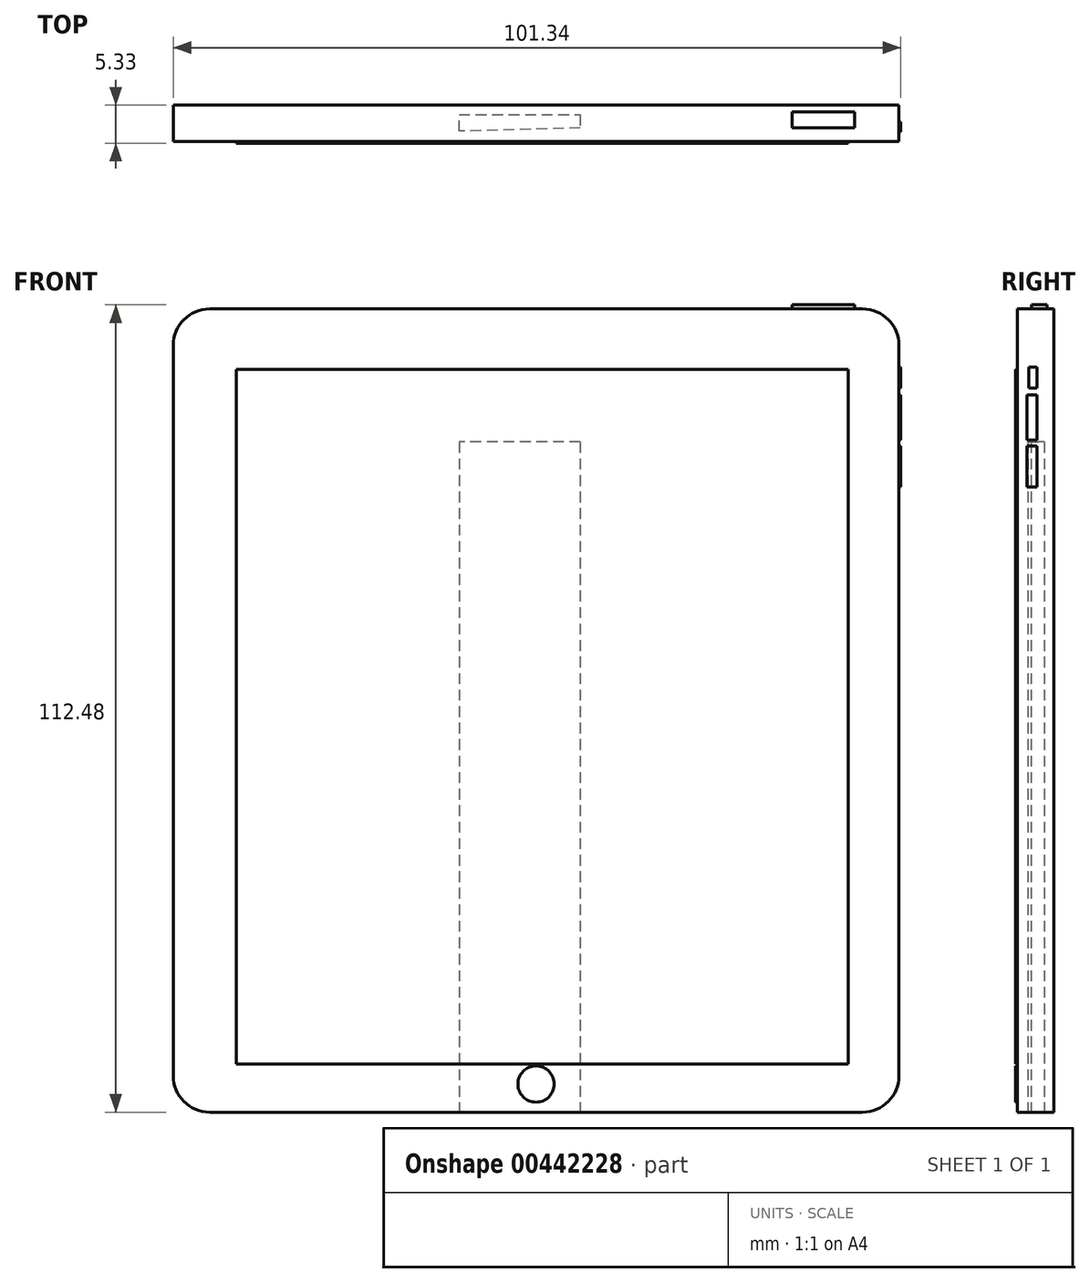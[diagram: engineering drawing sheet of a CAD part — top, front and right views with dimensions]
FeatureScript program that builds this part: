
annotation { "Feature Type Name" : "Feature", "Feature Type Description" : "" }
export const myFeature = defineFeature(function(context is Context, id is Id, definition is map)
    precondition{}
    {
        {
            var Q0;
            Q0=qCreatedBy(makeId("Front.planeOp"),FACE);
            var sketch = newSketch(context, id + "F0", { "sketchPlane" : qUnion([Q0])});
            skLineSegment(sketch, "E0.bottom", {"start": v(-45.46, 55.95) * mm, "end": v(45.46, 55.95) * mm});
            skLineSegment(sketch, "E0.top", {"start": v(-45.46, -55.95) * mm, "end": v(45.46, -55.95) * mm});
            skLineSegment(sketch, "E0.left", {"start": v(-50.54, 50.87) * mm, "end": v(-50.54, -50.87) * mm});
            skLineSegment(sketch, "E0.right", {"start": v(50.54, 50.87) * mm, "end": v(50.54, -50.87) * mm});
            skPoint(sketch, "E0.middle", {"position": v(0, 0) * mm});
            skPoint(sketch, "E1.visualSharp", {"position": v(-50.54, 55.95) * mm});
            skArc(sketch, "E1.filletArc", {"start": v(-45.46, 55.95) * mm, "mid": v(-49.05, 54.46) * mm, "end": v(-50.54, 50.87) * mm});
            skPoint(sketch, "E2.visualSharp", {"position": v(50.54, 55.95) * mm});
            skArc(sketch, "E2.filletArc", {"start": v(50.54, 50.87) * mm, "mid": v(49.05, 54.46) * mm, "end": v(45.46, 55.95) * mm});
            skPoint(sketch, "E3.visualSharp", {"position": v(50.54, -55.95) * mm});
            skArc(sketch, "E3.filletArc", {"start": v(45.46, -55.95) * mm, "mid": v(49.05, -54.46) * mm, "end": v(50.54, -50.87) * mm});
            skPoint(sketch, "E4.visualSharp", {"position": v(-50.54, -55.95) * mm});
            skArc(sketch, "E4.filletArc", {"start": v(-50.54, -50.87) * mm, "mid": v(-49.05, -54.46) * mm, "end": v(-45.46, -55.95) * mm});
            skCircle(sketch, "E5", {"center": v(0, -50.88) * mm, "radius": 2.74 * mm});
            skCircle(sketch, "E6", {"center": v(0, 50.88) * mm, "radius": 1.1 * mm});
            skSolve(sketch);
        }
        {
            var Q0;
            Q0 = qSketchRegion(id + "F0", true);
            var Q1;
            Q1=makeQuery(id+"F0.imprint","IMPRINT",FACE,{"disambiguationData":[TD([[makeQuery(id+"F0.imprint","IMPRINT",EDGE,{"derivedFrom":sQuery(id+"F0.wireOp",EDGE,"jizpzQJK-FtYb-snMM-lDZa-Pu40AYu2MoG9.bottom")}),-1.0]])]});
            var Q2;
            Q2=makeQuery(id+"F0.imprint","IMPRINT",FACE,{"disambiguationData":[TD([[makeQuery(id+"F0.imprint","IMPRINT",EDGE,{"derivedFrom":sQuery(id+"F0.wireOp",EDGE,"E5")}),1.0]])]});
            var Q3;
            Q3=makeQuery(id+"F0.imprint","IMPRINT",FACE,{"disambiguationData":[TD([[makeQuery(id+"F0.imprint","IMPRINT",EDGE,{"derivedFrom":sQuery(id+"F0.wireOp",EDGE,"E6")}),1.0]])]});
            extrude(context, id + "F1", {"entities" : qUnion([Q0, Q1, Q2, Q3]), "depth" : 5.08 * mm});
        }
        {
            var Q0;
            Q0=makeQuery(id+"F1.opExtrude","CAP_FACE",FACE,{"disambiguationData":[OSD([sQuery(id+"F0.wireOp",EDGE,"E0.bottom"),sQuery(id+"F0.wireOp",EDGE,"E0.top"),sQuery(id+"F0.wireOp",EDGE,"E0.left"),sQuery(id+"F0.wireOp",EDGE,"E0.right"),sQuery(id+"F0.wireOp",EDGE,"E1.filletArc"),sQuery(id+"F0.wireOp",EDGE,"E2.filletArc"),sQuery(id+"F0.wireOp",EDGE,"E3.filletArc"),sQuery(id+"F0.wireOp",EDGE,"E4.filletArc")])],"isStart":false});
            var sketch = newSketch(context, id + "F2", { "sketchPlane" : qUnion([Q0])});
            skLineSegment(sketch, "E7.bottom", {"start": v(-41.78, 47.56) * mm, "end": v(43.46, 47.56) * mm});
            skLineSegment(sketch, "E7.top", {"start": v(-41.78, -49.24) * mm, "end": v(43.46, -49.24) * mm});
            skLineSegment(sketch, "E7.left", {"start": v(-41.78, 47.56) * mm, "end": v(-41.78, -49.24) * mm});
            skLineSegment(sketch, "E7.right", {"start": v(43.46, 47.56) * mm, "end": v(43.46, -49.24) * mm});
            skCircle(sketch, "E8", {"center": v(0, -52.4) * mm, "radius": 2.27 * mm});
            skSolve(sketch);
        }
        {
            var Q0;
            Q0=makeQuery(id+"F2.imprint","IMPRINT",FACE,{"disambiguationData":[TD([[makeQuery(id+"F2.imprint","IMPRINT",EDGE,{"derivedFrom":sQuery(id+"F2.wireOp",EDGE,"E7.bottom")}),-1.0]])]});
            extrude(context, id + "F3", {"entities" : qUnion([Q0]), "operationType" : NewBodyOperationType.ADD, "depth" : 0.25 * mm});
        }
        {
            var Q0;
            Q0=makeQuery(id+"F1.opExtrude","SWEPT_FACE",FACE,{"disambiguationData":[OSD([sQuery(id+"F0.wireOp",EDGE,"E0.top")])]});
            var sketch = newSketch(context, id + "F4", { "sketchPlane" : qUnion([Q0])});
            skLineSegment(sketch, "E9", {"start": v(-10.72, 3.63) * mm, "end": v(-10.72, 1.34) * mm});
            skLineSegment(sketch, "E10", {"start": v(6.15, 1.34) * mm, "end": v(6.15, 3.19) * mm});
            skLineSegment(sketch, "E11", {"start": v(6.15, 3.19) * mm, "end": v(-10.72, 3.63) * mm});
            skLineSegment(sketch, "E12", {"start": v(-10.72, 1.34) * mm, "end": v(6.15, 1.34) * mm});
            skCircle(sketch, "E13", {"center": v(-40.95, 2.46) * mm, "radius": 1.96 * mm});
            skCircle(sketch, "E14", {"center": v(-35.96, 2.6) * mm, "radius": 1.7 * mm});
            skCircle(sketch, "E15", {"center": v(-31.16, 2.6) * mm, "radius": 1.58 * mm});
            skCircle(sketch, "E16", {"center": v(-26.62, 2.53) * mm, "radius": 1.52 * mm});
            skSolve(sketch);
        }
        {
            var Q0;
            Q0 = qSketchRegion(id + "F4", true);
            var sketch = newSketch(context, id + "F5", { "sketchPlane" : qUnion([Q0])});
            skSolve(sketch);
        }
        {
            var Q0;
            Q0=makeQuery(id+"F4.imprint","IMPRINT",FACE,{"disambiguationData":[TD([[makeQuery(id+"F4.imprint","IMPRINT",EDGE,{"derivedFrom":sQuery(id+"F4.wireOp",EDGE,"E9")}),1.0]])]});
            var Q1;
            Q1=makeQuery(id+"F5.imprint","IMPRINT",FACE,{"disambiguationData":[TD([[makeQuery(id+"F5.imprint","IMPRINT",EDGE,{"derivedFrom":makeQuery(id+"F4.imprint","IMPRINT",EDGE,{"derivedFrom":sQuery(id+"F4.wireOp",EDGE,"E13")})}),1.0]])]});
            var Q2;
            Q2=makeQuery(id+"F5.imprint","IMPRINT",FACE,{"disambiguationData":[TD([[makeQuery(id+"F5.imprint","IMPRINT",EDGE,{"derivedFrom":makeQuery(id+"F4.imprint","IMPRINT",EDGE,{"derivedFrom":sQuery(id+"F4.wireOp",EDGE,"E14")})}),1.0]])]});
            var Q3;
            Q3=makeQuery(id+"F5.imprint","IMPRINT",FACE,{"disambiguationData":[TD([[makeQuery(id+"F5.imprint","IMPRINT",EDGE,{"derivedFrom":makeQuery(id+"F4.imprint","IMPRINT",EDGE,{"derivedFrom":sQuery(id+"F4.wireOp",EDGE,"E15")})}),1.0]])]});
            var Q4;
            Q4=makeQuery(id+"F5.imprint","IMPRINT",FACE,{"disambiguationData":[TD([[makeQuery(id+"F5.imprint","IMPRINT",EDGE,{"derivedFrom":makeQuery(id+"F4.imprint","IMPRINT",EDGE,{"derivedFrom":sQuery(id+"F4.wireOp",EDGE,"E16")})}),1.0]])]});
            var Q5;
            Q5=sQuery(id+"F4.wireOp",EDGE,"E11");
            var Q6;
            Q6=sQuery(id+"F4.wireOp",EDGE,"E9");
            var Q7;
            Q7=sQuery(id+"F4.wireOp",EDGE,"E10");
            var Q8;
            Q8=sQuery(id+"F4.wireOp",EDGE,"E12");
            extrude(context, id + "F6", {"entities" : qUnion([Q0, Q1, Q2, Q3, Q4]), "surfaceEntities" : qUnion([Q5, Q6, Q7, Q8]), "oppositeDirection" : true, "depth" : 93.35 * mm});
        }
        {
            var Q0;
            Q0=makeQuery(id+"F1.opExtrude","SWEPT_FACE",FACE,{"disambiguationData":[OSD([sQuery(id+"F0.wireOp",EDGE,"E0.bottom")])]});
            var sketch = newSketch(context, id + "F7", { "sketchPlane" : qUnion([Q0])});
            skCircle(sketch, "E17", {"center": v(-41, -2.61) * mm, "radius": 1.52 * mm});
            skLineSegment(sketch, "E18.bottom", {"start": v(44.36, -0.97) * mm, "end": v(35.64, -0.97) * mm});
            skLineSegment(sketch, "E18.top", {"start": v(44.36, -3.16) * mm, "end": v(35.64, -3.16) * mm});
            skLineSegment(sketch, "E18.left", {"start": v(44.36, -0.97) * mm, "end": v(44.36, -3.16) * mm});
            skLineSegment(sketch, "E18.right", {"start": v(35.64, -0.97) * mm, "end": v(35.64, -3.16) * mm});
            skLineSegment(sketch, "E19.bottom", {"start": v(-1.77, -3.7) * mm, "end": v(2.1, -3.7) * mm});
            skLineSegment(sketch, "E19.top", {"start": v(-1.77, -3.1) * mm, "end": v(2.1, -3.1) * mm});
            skLineSegment(sketch, "E19.left", {"start": v(-1.77, -3.7) * mm, "end": v(-1.77, -3.1) * mm});
            skLineSegment(sketch, "E19.right", {"start": v(2.1, -3.7) * mm, "end": v(2.1, -3.1) * mm});
            skSolve(sketch);
        }
        {
            var Q0;
            Q0=makeQuery(id+"F7.imprint","IMPRINT",FACE,{"disambiguationData":[TD([[makeQuery(id+"F7.imprint","IMPRINT",EDGE,{"derivedFrom":sQuery(id+"F7.wireOp",EDGE,"E18.bottom")}),1.0]])]});
            var Q1;
            Q1=sQuery(id+"F7.wireOp",EDGE,"E18.bottom");
            var Q2;
            Q2=sQuery(id+"F7.wireOp",EDGE,"E18.left");
            var Q3;
            Q3=sQuery(id+"F7.wireOp",EDGE,"E18.top");
            var Q4;
            Q4=sQuery(id+"F7.wireOp",EDGE,"E18.right");
            extrude(context, id + "F8", {"entities" : qUnion([Q0]), "operationType" : NewBodyOperationType.ADD, "surfaceEntities" : qUnion([Q1, Q2, Q3, Q4]), "depth" : 0.57 * mm});
        }
        {
            var Q0;
            Q0=makeQuery(id+"F1.opExtrude","CAP_FACE",FACE,{"disambiguationData":[OSD([sQuery(id+"F0.wireOp",EDGE,"E0.bottom"),sQuery(id+"F0.wireOp",EDGE,"E0.top"),sQuery(id+"F0.wireOp",EDGE,"E0.left"),sQuery(id+"F0.wireOp",EDGE,"E0.right"),sQuery(id+"F0.wireOp",EDGE,"E1.filletArc"),sQuery(id+"F0.wireOp",EDGE,"E2.filletArc"),sQuery(id+"F0.wireOp",EDGE,"E3.filletArc"),sQuery(id+"F0.wireOp",EDGE,"E4.filletArc")])],"isStart":false});
            var sketch = newSketch(context, id + "F9", { "sketchPlane" : qUnion([Q0])});
            skCircle(sketch, "E20", {"center": v(0, -52.03) * mm, "radius": 2.53 * mm});
            skPoint(sketch, "E20.centerSnap0", {"position": v(0, -55.95) * mm});
            skSolve(sketch);
        }
        {
            var Q0;
            Q0 = qSketchRegion(id + "F9", true);
            extrude(context, id + "F10", {"entities" : qUnion([Q0]), "operationType" : NewBodyOperationType.ADD, "depth" : 0.25 * mm});
        }
        {
            var Q0;
            Q0=makeQuery(id+"F1.opExtrude","SWEPT_FACE",FACE,{"disambiguationData":[OSD([sQuery(id+"F0.wireOp",EDGE,"E0.right")])]});
            var sketch = newSketch(context, id + "F11", { "sketchPlane" : qUnion([Q0])});
            skLineSegment(sketch, "E21.bottom", {"start": v(-3.74, 44) * mm, "end": v(-2.37, 44) * mm});
            skLineSegment(sketch, "E21.top", {"start": v(-3.74, 37.7) * mm, "end": v(-2.37, 37.7) * mm});
            skLineSegment(sketch, "E21.left", {"start": v(-3.74, 44) * mm, "end": v(-3.74, 37.7) * mm});
            skLineSegment(sketch, "E21.right", {"start": v(-2.37, 44) * mm, "end": v(-2.37, 37.7) * mm});
            skLineSegment(sketch, "E22.bottom", {"start": v(-3.78, 36.87) * mm, "end": v(-2.37, 36.87) * mm});
            skLineSegment(sketch, "E22.top", {"start": v(-3.78, 31.14) * mm, "end": v(-2.37, 31.14) * mm});
            skLineSegment(sketch, "E22.left", {"start": v(-3.78, 36.87) * mm, "end": v(-3.78, 31.14) * mm});
            skLineSegment(sketch, "E22.right", {"start": v(-2.37, 36.87) * mm, "end": v(-2.37, 31.14) * mm});
            skLineSegment(sketch, "E23.bottom", {"start": v(-3.54, 47.84) * mm, "end": v(-2.37, 47.84) * mm});
            skLineSegment(sketch, "E23.top", {"start": v(-3.54, 44.9) * mm, "end": v(-2.37, 44.9) * mm});
            skLineSegment(sketch, "E23.left", {"start": v(-3.54, 47.84) * mm, "end": v(-3.54, 44.9) * mm});
            skLineSegment(sketch, "E23.right", {"start": v(-2.37, 47.84) * mm, "end": v(-2.37, 44.9) * mm});
            skSolve(sketch);
        }
        {
            var Q0;
            Q0 = qSketchRegion(id + "F11", true);
            extrude(context, id + "F12", {"entities" : qUnion([Q0]), "operationType" : NewBodyOperationType.ADD, "depth" : 0.25 * mm});
        }
    });
